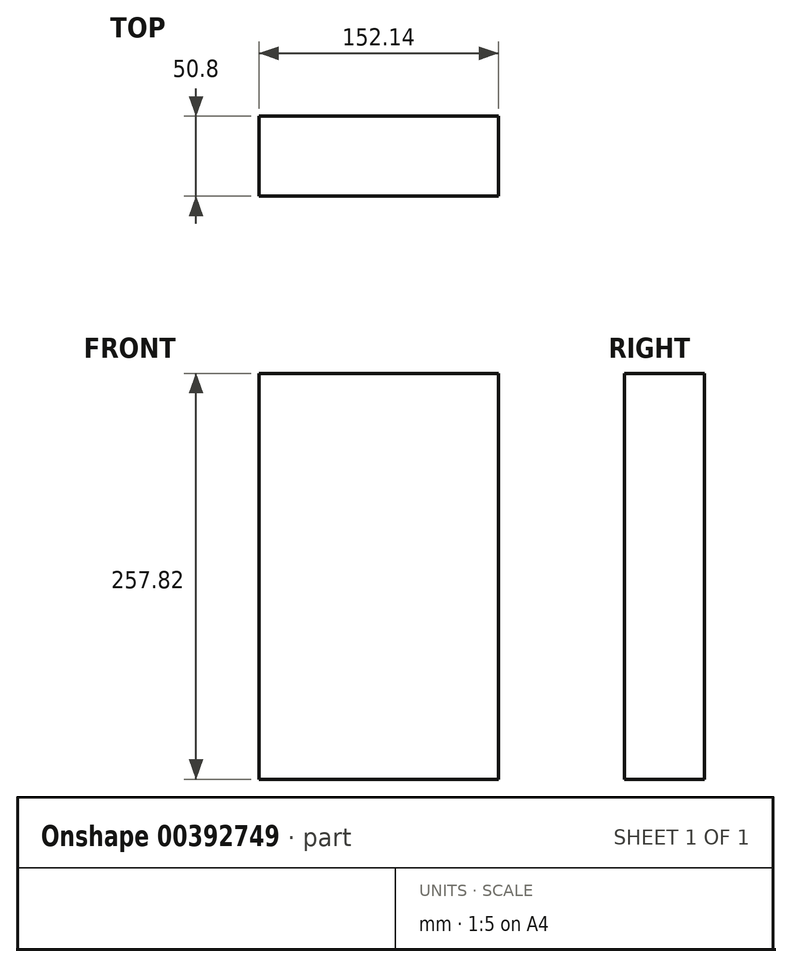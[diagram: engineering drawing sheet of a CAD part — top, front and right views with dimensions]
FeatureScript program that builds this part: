
annotation { "Feature Type Name" : "Feature", "Feature Type Description" : "" }
export const myFeature = defineFeature(function(context is Context, id is Id, definition is map)
    precondition{}
    {
        {
            var Q0;
            Q0=qCreatedBy(makeId("Front.planeOp"),FACE);
            var sketch = newSketch(context, id + "F0", { "sketchPlane" : qUnion([Q0])});
            skLineSegment(sketch, "E0.bottom", {"start": v(-76.07, -128.9) * mm, "end": v(76.07, -128.9) * mm});
            skLineSegment(sketch, "E0.top", {"start": v(-76.07, 128.9) * mm, "end": v(76.07, 128.9) * mm});
            skLineSegment(sketch, "E0.left", {"start": v(-76.07, -128.9) * mm, "end": v(-76.07, 128.9) * mm});
            skLineSegment(sketch, "E0.right", {"start": v(76.07, -128.9) * mm, "end": v(76.07, 128.9) * mm});
            skPoint(sketch, "E0.middle", {"position": v(0, 0) * mm});
            skSolve(sketch);
        }
        {
            var Q0;
            Q0 = qSketchRegion(id + "F0", true);
            extrude(context, id + "F1", {"entities" : qUnion([Q0]), "endBound" : BoundingType.SYMMETRIC, "depth" : 50.8 * mm});
        }
    });
